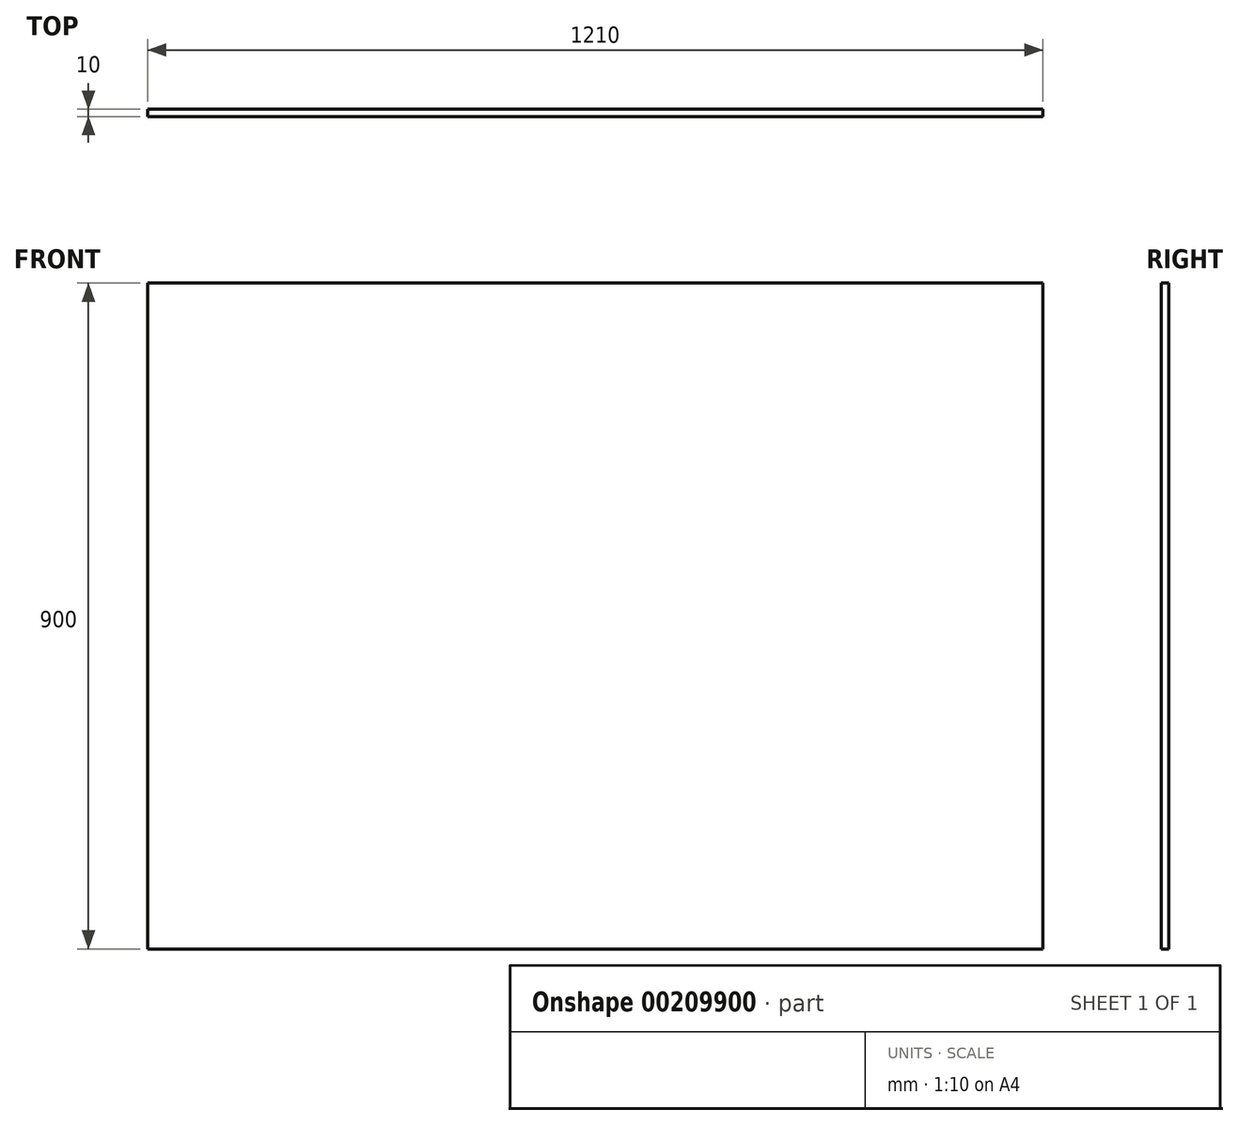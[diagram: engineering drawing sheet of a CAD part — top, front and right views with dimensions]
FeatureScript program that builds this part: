
annotation { "Feature Type Name" : "Feature", "Feature Type Description" : "" }
export const myFeature = defineFeature(function(context is Context, id is Id, definition is map)
    precondition{}
    {
        {
            var Q0;
            Q0=qCreatedBy(makeId("Front.planeOp"),FACE);
            var sketch = newSketch(context, id + "F0", { "sketchPlane" : qUnion([Q0])});
            skLineSegment(sketch, "E0.bottom", {"start": v(-605, 450) * mm, "end": v(605, 450) * mm});
            skLineSegment(sketch, "E0.top", {"start": v(-605, -450) * mm, "end": v(605, -450) * mm});
            skLineSegment(sketch, "E0.left", {"start": v(-605, 450) * mm, "end": v(-605, -450) * mm});
            skLineSegment(sketch, "E0.right", {"start": v(605, 450) * mm, "end": v(605, -450) * mm});
            skPoint(sketch, "E0.middle", {"position": v(0, 0) * mm});
            skSolve(sketch);
        }
        {
            var Q0;
            Q0=makeQuery(id+"F0.imprint","IMPRINT",FACE,{"disambiguationData":[TD([[makeQuery(id+"F0.imprint","IMPRINT",EDGE,{"derivedFrom":sQuery(id+"F0.wireOp",EDGE,"E0.bottom")}),-1.0]])]});
            extrude(context, id + "F1", {"entities" : qUnion([Q0]), "depth" : 10 * mm});
        }
    });
